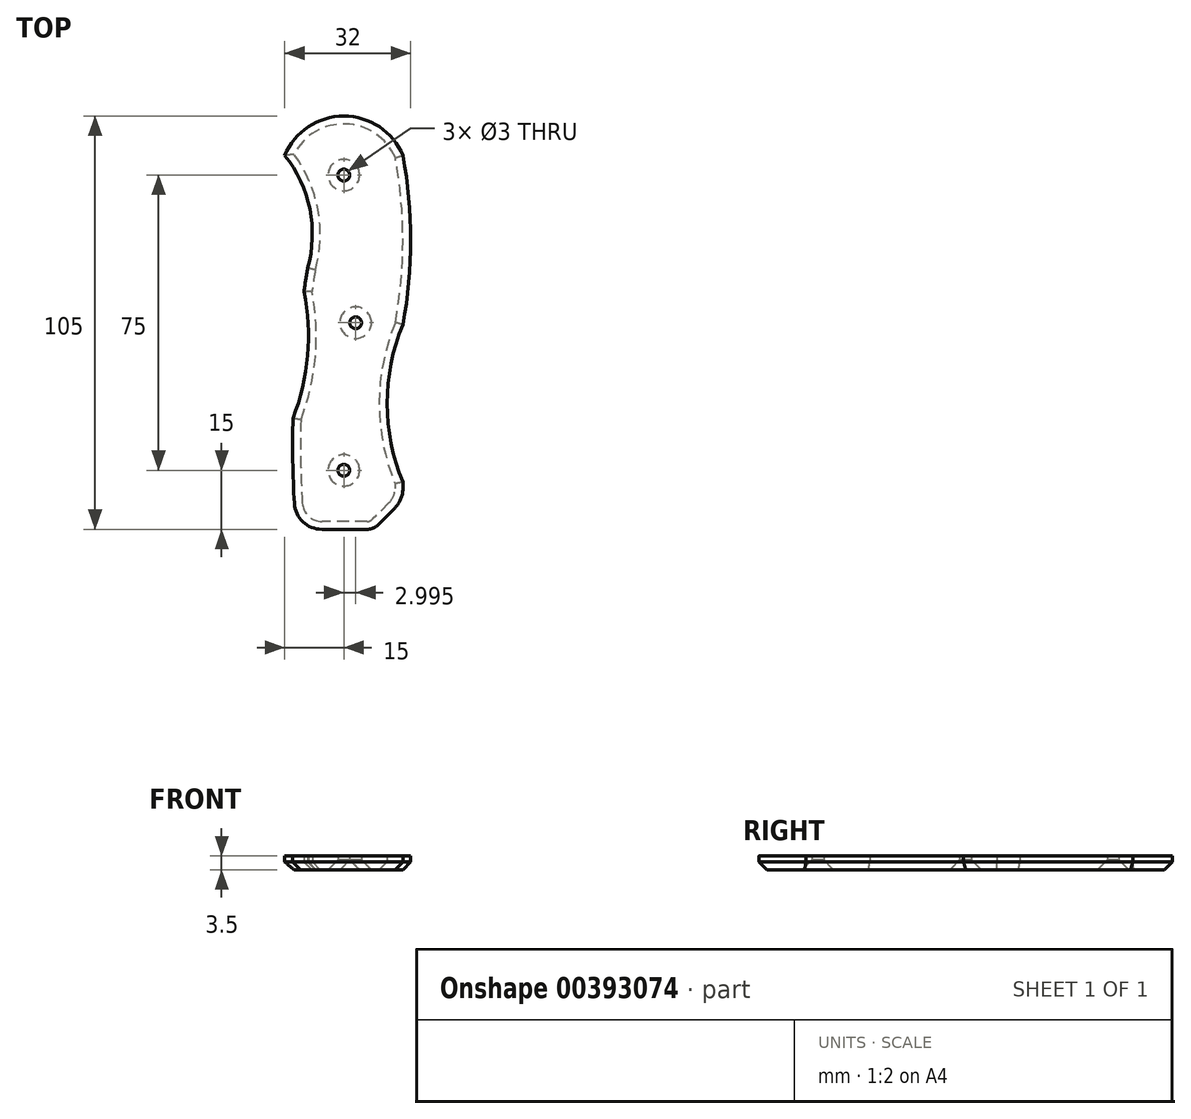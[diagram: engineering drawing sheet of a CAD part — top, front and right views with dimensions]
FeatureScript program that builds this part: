
annotation { "Feature Type Name" : "Feature", "Feature Type Description" : "" }
export const myFeature = defineFeature(function(context is Context, id is Id, definition is map)
    precondition{}
    {
        {
            var Q0;
            Q0=qCreatedBy(makeId("Top.planeOp"),FACE);
            var sketch = newSketch(context, id + "F0", { "sketchPlane" : qUnion([Q0])});
            skLineSegment(sketch, "E0.bottom", {"start": v(15.42, 23) * mm, "end": v(26.88, 23) * mm});
            skLineSegment(sketch, "E0.left", {"start": v(6, 0) * mm, "end": v(6, 118) * mm});
            skLineSegment(sketch, "E0.right", {"start": v(36, 10.36) * mm, "end": v(36, 118) * mm});
            skCircle(sketch, "E1", {"center": v(21, 113) * mm, "radius": 1.5 * mm});
            skPoint(sketch, "E1.centerSnap0", {"position": v(21, 128) * mm});
            skLineSegment(sketch, "E2", {"start": v(36, 78) * mm, "end": v(6, 78) * mm, "construction": true});
            skArc(sketch, "E3", {"start": v(36, 118) * mm, "mid": v(21, 128) * mm, "end": v(6, 118) * mm});
            skLineSegment(sketch, "E4", {"start": v(6, 118) * mm, "end": v(36, 118) * mm, "construction": true});
            skArc(sketch, "E5", {"start": v(11.81, 89.36) * mm, "mid": v(12.36, 104.38) * mm, "end": v(6, 118) * mm});
            skArc(sketch, "E6", {"start": v(11.81, 89.36) * mm, "mid": v(8.42, 59.58) * mm, "end": v(8.43, 29.6) * mm});
            skArc(sketch, "E7", {"start": v(8.08, 51.22) * mm, "mid": v(11.79, 67.12) * mm, "end": v(10.86, 83.43) * mm});
            skPoint(sketch, "E8.newPointA", {"position": v(11.81, 0) * mm});
            skPoint(sketch, "E8.newPointB", {"position": v(3, 23) * mm});
            skArc(sketch, "E8.filletArc", {"start": v(8.43, 29.6) * mm, "mid": v(10.61, 24.91) * mm, "end": v(15.42, 23) * mm});
            skPoint(sketch, "E9.visualSharp", {"position": v(36, 23) * mm});
            skLineSegment(sketch, "E10", {"start": v(29.7, 24.17) * mm, "end": v(33.95, 28.41) * mm});
            skArc(sketch, "E11.filletArc", {"start": v(26.88, 23) * mm, "mid": v(28.4, 23.3) * mm, "end": v(29.7, 24.17) * mm});
            skArc(sketch, "E12.filletArc", {"start": v(33.95, 28.41) * mm, "mid": v(35.47, 30.69) * mm, "end": v(36, 33.36) * mm});
            skArc(sketch, "E13", {"start": v(36, 75) * mm, "mid": v(32, 55) * mm, "end": v(36, 35) * mm});
            skArc(sketch, "E14", {"start": v(36, 75) * mm, "mid": v(38, 96.5) * mm, "end": v(36, 118) * mm});
            skLineSegment(sketch, "E15", {"start": v(21, 128) * mm, "end": v(21, 23) * mm, "construction": true});
            skPoint(sketch, "E15.endSnap0", {"position": v(21.15, 23) * mm});
            skLineSegment(sketch, "E16", {"start": v(36.1, 75.5) * mm, "end": v(11.9, 75.5) * mm, "construction": true});
            skPoint(sketch, "E16.endSnap0", {"position": v(21, 75.5) * mm});
            skCircle(sketch, "E17.MirrorC", {"center": v(21, 38) * mm, "radius": 1.5 * mm});
            skCircle(sketch, "E18", {"center": v(24, 75.5) * mm, "radius": 1.5 * mm});
            skSolve(sketch);
        }
        {
            var Q0;
            Q0=makeQuery(id+"F0.imprint","IMPRINT",FACE,{"disambiguationData":[TD([[makeQuery(id+"F0.imprint","IMPRINT",EDGE,{"derivedFrom":sQuery(id+"F0.wireOp",EDGE,"E1")}),-1.0]])]});
            var Q1;
            {var subQ0=sQuery(id+"F0.wireOp",EDGE,"E14");Q1=makeQuery(id+"F0.imprint","IMPRINT",FACE,{"disambiguationData":[TD([[makeQuery(id+"F0.imprint","IMPRINT",EDGE,{"derivedFrom":subQ0}),1.0]])]});}
            extrude(context, id + "F1", {"entities" : qUnion([Q0, Q1]), "depth" : 3.5 * mm});
        }
        {
            var Q0;
            {var subQ0=sQuery(id+"F0.wireOp",EDGE,"E6");Q0=makeQuery(id+"F1.opExtrude","CAP_EDGE",EDGE,{"disambiguationData":[OSD([subQ0]),TDD([makeQuery(id+"F0.imprint","IMPRINT",EDGE,{"disambiguationData":[TD([[makeQuery(id+"F0.imprint","INTERSECT",VERTEX,{"derivedFrom":[subQ0,sQuery(id+"F0.wireOp",EDGE,"E8.filletArc")]}),1.0]])],"derivedFrom":subQ0})])],"isStart":true});}
            var Q1;
            Q1=makeQuery(id+"F1.opExtrude","CAP_EDGE",EDGE,{"disambiguationData":[OSD([sQuery(id+"F0.wireOp",EDGE,"E13")])],"isStart":true});
            var Q2;
            Q2=makeQuery(id+"F1.opExtrude","CAP_EDGE",EDGE,{"disambiguationData":[OSD([sQuery(id+"F0.wireOp",EDGE,"E14")])],"isStart":true});
            var Q3;
            Q3=makeQuery(id+"F1.opExtrude","CAP_EDGE",EDGE,{"disambiguationData":[OSD([sQuery(id+"F0.wireOp",EDGE,"E3")])],"isStart":true});
            var Q4;
            Q4=makeQuery(id+"F1.opExtrude","CAP_EDGE",EDGE,{"disambiguationData":[OSD([sQuery(id+"F0.wireOp",EDGE,"E5")])],"isStart":true});
            var Q5;
            Q5=makeQuery(id+"F1.opExtrude","CAP_EDGE",EDGE,{"disambiguationData":[OSD([sQuery(id+"F0.wireOp",EDGE,"E7")])],"isStart":true});
            var Q6;
            {var subQ0=sQuery(id+"F0.wireOp",EDGE,"E6");Q6=makeQuery(id+"F1.opExtrude","CAP_EDGE",EDGE,{"disambiguationData":[OSD([subQ0]),TDD([makeQuery(id+"F0.imprint","IMPRINT",EDGE,{"disambiguationData":[TD([[makeQuery(id+"F0.imprint","INTERSECT",VERTEX,{"derivedFrom":[sQuery(id+"F0.wireOp",EDGE,"E5"),subQ0]}),-1.0]])],"derivedFrom":subQ0})])],"isStart":true});}
            chamfer(context, id + "F2", {"entities" : qUnion([Q0, Q1, Q2, Q3, Q4, Q5, Q6]), "width" : 2 * mm, "tangentPropagation" : true});
        }
        {
            var Q0;
            Q0=makeQuery(id+"F1.opExtrude","CAP_EDGE",EDGE,{"disambiguationData":[OSD([sQuery(id+"F0.wireOp",EDGE,"E1")])],"isStart":true});
            var Q1;
            Q1=makeQuery(id+"F1.opExtrude","CAP_EDGE",EDGE,{"disambiguationData":[OSD([sQuery(id+"F0.wireOp",EDGE,"E17.MirrorC")])],"isStart":true});
            var Q2;
            Q2=makeQuery(id+"F1.opExtrude","CAP_EDGE",EDGE,{"disambiguationData":[OSD([sQuery(id+"F0.wireOp",EDGE,"E18")])],"isStart":true});
            chamfer(context, id + "F3", {"entities" : qUnion([Q0, Q1, Q2]), "width" : 2.5 * mm, "tangentPropagation" : true});
        }
    });
